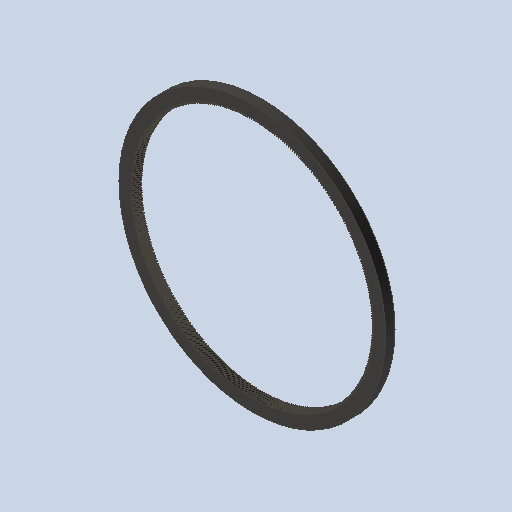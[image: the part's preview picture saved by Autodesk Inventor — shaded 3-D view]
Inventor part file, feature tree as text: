
AUTODESK INVENTOR PART (.ipt)
format: ipt  version: 2023 (Build 270158000, 158)  size: 3,941,376 bytes
history: native  units: mm (DEFAULTED — no unit token found)
features: plane x3, other x3, sketch x2, extrude x1
ambient origin geometry x8: Origin, YZ Plane, XZ Plane, XY Plane, X Axis, Y Axis, Z Axis, Center Point
bodies: Solid1 (feature_tree)
feature tree (9):
  extrude  "Extrusion1"  Depth=15.0mm TaperAngle=0.0deg
  plane  "Work Plane2"
  plane  "Work Plane8"
  plane  "Work Plane9"
  other  "Spur Gear"
  sketch  "Sketch1"  dims[d0=425.271304mm d1=15.0mm d2=0.0mm]
  sketch  "Sketch2"  dims[d3=384.168176mm d4=10.0mm d5=0.0mm d16=101.6mm d17=0.0mm d34=0.087025mm d39=0.0mm d45=0.0mm d47=101.6mm d50=0.0mm d51=0.0mm d52=101.6mm]
  other  "Srf1"
  other  "Pitch Diameter"
